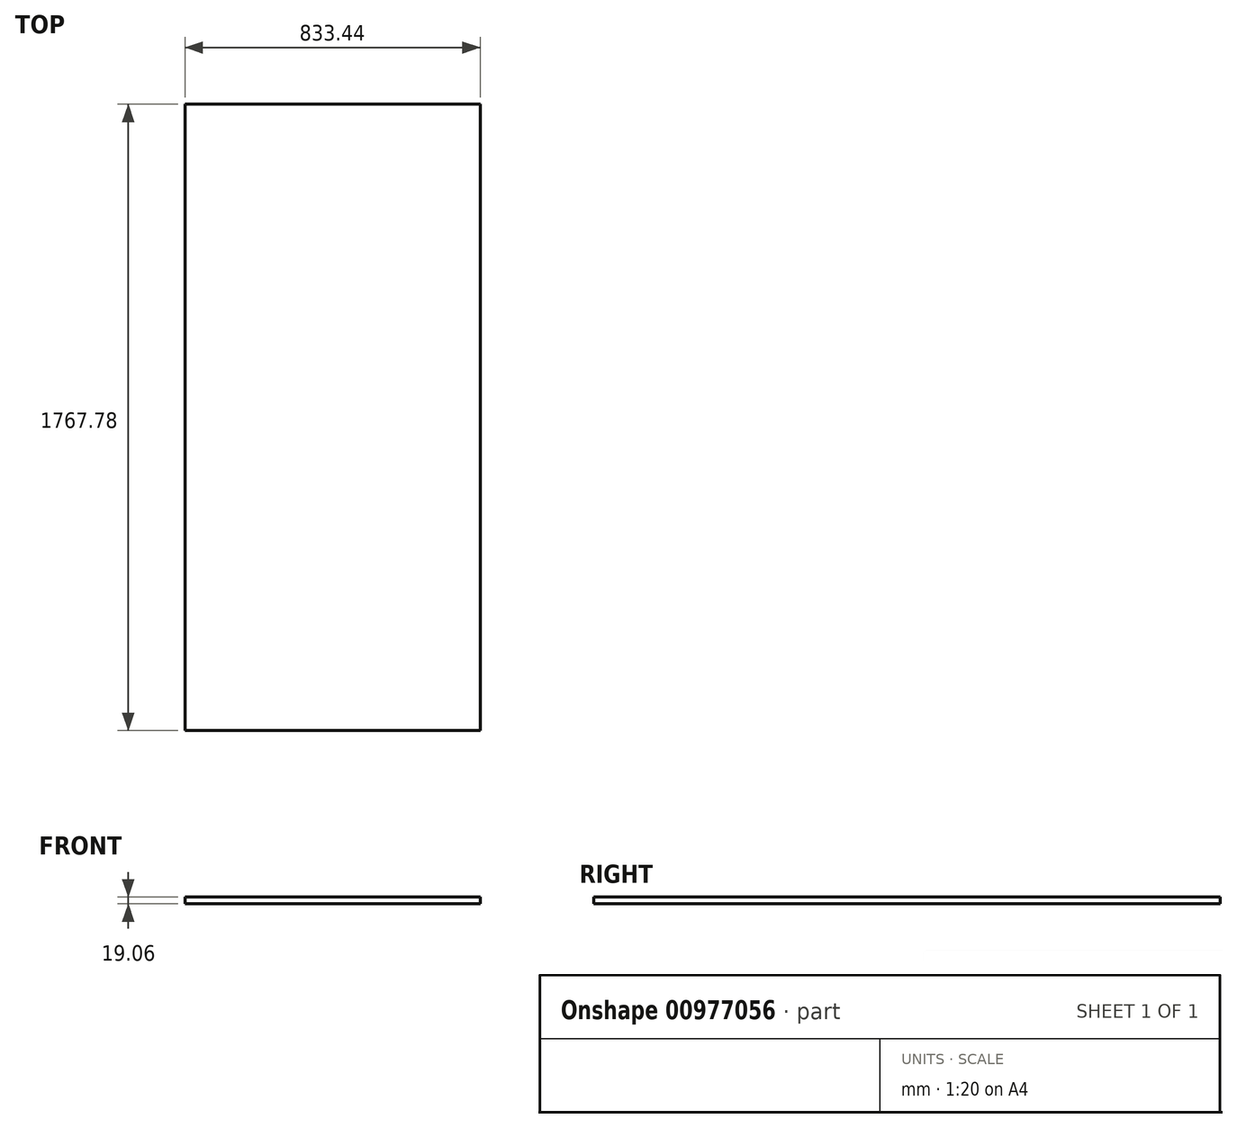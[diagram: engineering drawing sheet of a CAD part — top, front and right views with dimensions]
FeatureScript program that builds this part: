
annotation { "Feature Type Name" : "Feature", "Feature Type Description" : "" }
export const myFeature = defineFeature(function(context is Context, id is Id, definition is map)
    precondition{}
    {
        {
            var Q0;
            Q0=qCreatedBy(makeId("Front.planeOp"),FACE);
            var sketch = newSketch(context, id + "F0", { "sketchPlane" : qUnion([Q0])});
            skLineSegment(sketch, "E0.bottom", {"start": v(416.72, -9.52) * mm, "end": v(-416.72, -9.53) * mm});
            skLineSegment(sketch, "E0.top", {"start": v(416.72, 9.53) * mm, "end": v(-416.72, 9.52) * mm});
            skLineSegment(sketch, "E0.left", {"start": v(416.72, -9.52) * mm, "end": v(416.72, 9.53) * mm});
            skLineSegment(sketch, "E0.right", {"start": v(-416.72, -9.53) * mm, "end": v(-416.72, 9.52) * mm});
            skPoint(sketch, "E0.middle", {"position": v(0, 0) * mm});
            skSolve(sketch);
        }
        {
            var Q0;
            Q0 = qSketchRegion(id + "F0", true);
            extrude(context, id + "F1", {"entities" : qUnion([Q0]), "endBound" : BoundingType.SYMMETRIC, "depth" : 1767.8 * mm, "offsetDistance" : 25.4 * mm});
        }
    });
